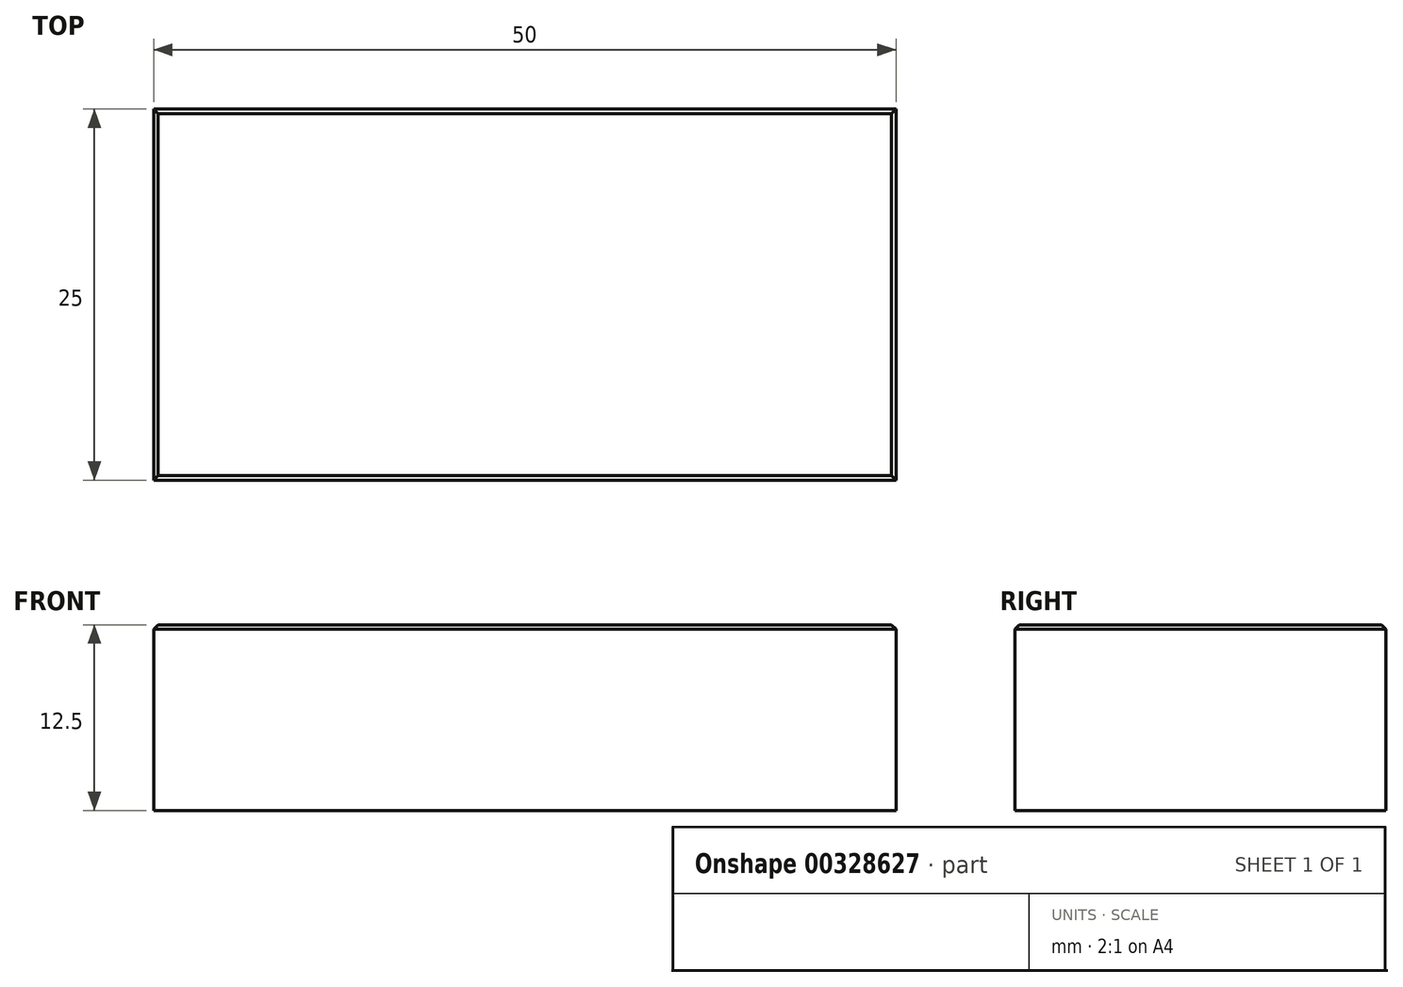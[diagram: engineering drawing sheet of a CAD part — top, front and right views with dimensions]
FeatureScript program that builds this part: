
annotation { "Feature Type Name" : "Feature", "Feature Type Description" : "" }
export const myFeature = defineFeature(function(context is Context, id is Id, definition is map)
    precondition{}
    {
        {
            var Q0;
            Q0=qCreatedBy(makeId("Top.planeOp"),FACE);
            var sketch = newSketch(context, id + "F0", { "sketchPlane" : qUnion([Q0])});
            skLineSegment(sketch, "E0.bottom", {"start": v(25, 12.5) * mm, "end": v(-25, 12.5) * mm});
            skLineSegment(sketch, "E0.top", {"start": v(25, -12.5) * mm, "end": v(-25, -12.5) * mm});
            skLineSegment(sketch, "E0.left", {"start": v(25, 12.5) * mm, "end": v(25, -12.5) * mm});
            skLineSegment(sketch, "E0.right", {"start": v(-25, 12.5) * mm, "end": v(-25, -12.5) * mm});
            skPoint(sketch, "E0.middle", {"position": v(0, 0) * mm});
            skSolve(sketch);
        }
        {
            var Q0;
            Q0=qSketchRegion(id+"F0",true);
            extrude(context, id + "F1", {"entities" : qUnion([Q0]), "oppositeDirection" : true, "depth" : 12.5 * mm});
        }
        {
            var Q0;
            Q0=makeQuery(id+"F1.opExtrude","CAP_FACE",FACE,{"disambiguationData":[OSD([sQuery(id+"F0.wireOp",EDGE,"E0.bottom"),sQuery(id+"F0.wireOp",EDGE,"E0.top"),sQuery(id+"F0.wireOp",EDGE,"E0.left"),sQuery(id+"F0.wireOp",EDGE,"E0.right")])],"isStart":true});
            chamfer(context, id + "F2", {"entities" : qUnion([Q0]), "width" : .3 * mm, "tangentPropagation" : true});
        }
    });
